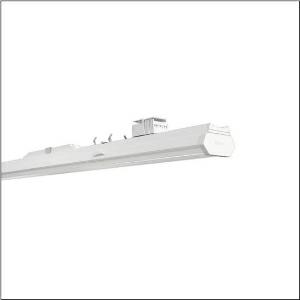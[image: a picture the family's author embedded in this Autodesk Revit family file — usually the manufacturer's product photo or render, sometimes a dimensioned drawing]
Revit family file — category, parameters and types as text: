
# Revit family: licross_r__11_protected_ho_51tp11cn4dxrd_fb9c
name_source: partatom
category: Lighting Fixtures
units: mm (PartAtom-declared; Revit-internal decimal feet)

## family parameters
Cut with Voids When Loaded = No
Host = Face
Light Source = No
Part Type = Normal
Room Calculation Point = No
Round Connector Dimension = Use Diameter
Shared = No

## types (1)
- --- (1 x LED, 3360 lm, 21.6 W, 4000K)
    Apparent Load = 22 VA
    CIE Flux Codes = 84 94 98 99 100
    Color Rendering = 80
    Color Temperature = 4000K
    Default Elevation = 1800 mm
    Description = Licross® 11 Protected HOluminaire insert, length: 1.500mm, width: 90mm, height: 101mm, LED rated luminous flux: 13.240lm, light colour: 840, control gear: ON/OFF Multilumen, CLOi, control gear: ECG Multilumen, with plug, 6-pole, with phase selection, mains connection: 220..240V, AC/DC, 0/50..60Hz, without changeover relay, for emergency light function, for central battery installations according to DIN EN 60598-2-22, halogen-free wiring, primary optical cover: cover, of PMMA, light emission: direct with ceiling illumination distribution, protection rating (complete): IP64, insulation class (complete): insulation class I (protective earthing), certification: CE, ENEC, VDE, protection symbol: D if used in an environment without relevant dust loads with corresponding accessories, permissible ambient temperature for indoor applications: -35..+40°C, standard: EN 60598-2-22, reducing of maximum allowable ambient temperature of 5°C with ceiling mounting, corresponds to IFS (International Featured Standards) requirements for safety and quality in the food industry, packaging unit: 1 piece
    Height = 92 mm
    Lamp = 1 x LED
    Lamp Light Flux = 3360 lm
    Lamp Power = 21.6 W
    Lamp count = 1
    Length = 1500 mm
    Luminous efficacy = 156 lm/W
    Manufacturer = Siteco
    ModVariant = No
    Model = 51TP11CN4DXRD
    Mounting Place = Ceiling
    Mounting Type = Pendant
    Number of Poles = 1
    OnlyDefault = Yes
    Power Factor = 1
    Product Name = Licross® 11 Protected HO
    Product group = luminaire insert
    ProductGroupID = 902
    Protection Class = Protection class I
    Protection Degree = IP 64
    RLX_Detail_Level = 1
    RlxData = <blob elided: 22149 chars, md5=b08fe0e8>
    Socket = socket
    Standby Power = 0 W
    System Light Flux = 3360 lm
    System Power = 22 W
    Type Comments = : DC mode (central or group accumulator) initial emergency light level
    Type Image = l_1256148.jpg
    URL = http://relux.com
    VarID = @adj_134647
    Voltage = 0 V
    Weight = 0.00 kg
    Width = 88 mm

## geometry (parser evidence)
native form markers: Blend x4, Sweep x10
no freeform markers — native parametric forms only
